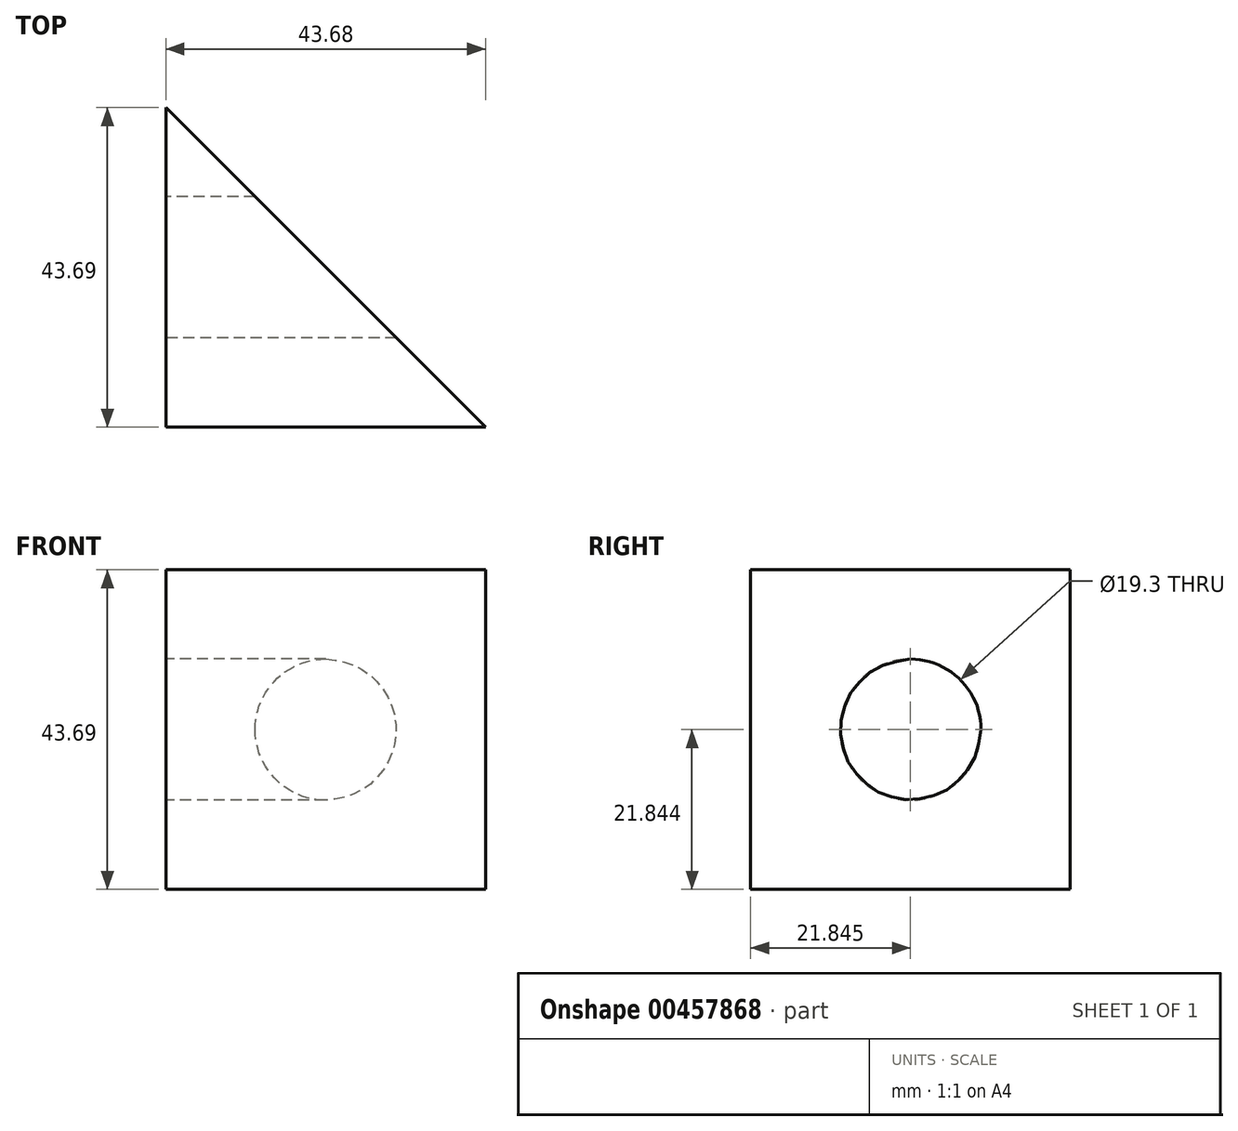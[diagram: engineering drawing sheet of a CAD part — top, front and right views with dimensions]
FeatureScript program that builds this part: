
annotation { "Feature Type Name" : "Feature", "Feature Type Description" : "" }
export const myFeature = defineFeature(function(context is Context, id is Id, definition is map)
    precondition{}
    {
        {
            var Q0;
            Q0=qCreatedBy(makeId("Top.planeOp"),FACE);
            var sketch = newSketch(context, id + "F0", { "sketchPlane" : qUnion([Q0])});
            skLineSegment(sketch, "E0.top", {"start": v(-57.02, 2.48) * mm, "end": v(-13.34, 2.48) * mm});
            skLineSegment(sketch, "E0.left", {"start": v(-57.02, 46.17) * mm, "end": v(-57.02, 2.48) * mm});
            skLineSegment(sketch, "E1", {"start": v(-57.02, 46.17) * mm, "end": v(-13.34, 2.48) * mm});
            skSolve(sketch);
        }
        {
            var Q0;
            Q0=makeQuery(id+"F0.imprint","IMPRINT",FACE,{"disambiguationData":[TD([[makeQuery(id+"F0.imprint","IMPRINT",EDGE,{"derivedFrom":sQuery(id+"F0.wireOp",EDGE,"E0.top")}),1.0]])]});
            extrude(context, id + "F1", {"entities" : qUnion([Q0]), "depth" : 43.69 * mm});
        }
        {
            var Q0;
            Q0=makeQuery(id+"F1.opExtrude","SWEPT_FACE",FACE,{"disambiguationData":[OSD([sQuery(id+"F0.wireOp",EDGE,"E0.left")])]});
            var sketch = newSketch(context, id + "F2", { "sketchPlane" : qUnion([Q0])});
            skCircle(sketch, "E2", {"center": v(-24.32, 21.84) * mm, "radius": 9.65 * mm});
            skSolve(sketch);
        }
        {
            var Q0;
            Q0=makeQuery(id+"F2.imprint","IMPRINT",FACE,{"disambiguationData":[TD([[makeQuery(id+"F2.imprint","IMPRINT",EDGE,{"derivedFrom":sQuery(id+"F2.wireOp",EDGE,"E2")}),1.0]])]});
            extrude(context, id + "F3", {"entities" : qUnion([Q0]), "operationType" : NewBodyOperationType.REMOVE, "endBound" : BoundingType.THROUGH_ALL, "oppositeDirection" : true, "depth" : 25.4 * mm});
        }
    });
